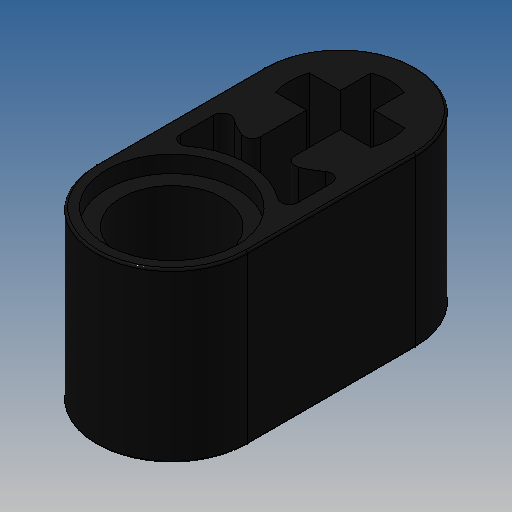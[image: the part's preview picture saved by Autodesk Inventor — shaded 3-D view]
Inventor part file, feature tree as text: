
AUTODESK INVENTOR PART (.ipt)
format: ipt  version: 2025 (Build 290162010, 162A)  size: 190,464 bytes
history: native  units: mm
features: extrude x2, sketch x2, mirror x1, fillet x1
ambient origin geometry x8: Origin, YZ Plane, XZ Plane, XY Plane, X Axis, Y Axis, Z Axis, Center Point
bodies: Solid1 (feature_tree)
feature tree (6):
  extrude  "Extrusion1"  Depth=6.4mm
  extrude  "Extrusion7"  Depth=7.2mm
  mirror  "Mirror1"
  fillet  "Fillet1"  Radius=8.0mm
  sketch  "Sketch1"  dims[d8=4.8mm d9=6.4mm]
  sketch  "Sketch6"  dims[d14=8.0mm d15=0.0mm d32=7.2mm d34=8.0mm d36=0.8mm d41=0.8mm d42=0.0mm d45=0.1mm d46=0.4mm d52=1.6mm d53=6.2mm]
